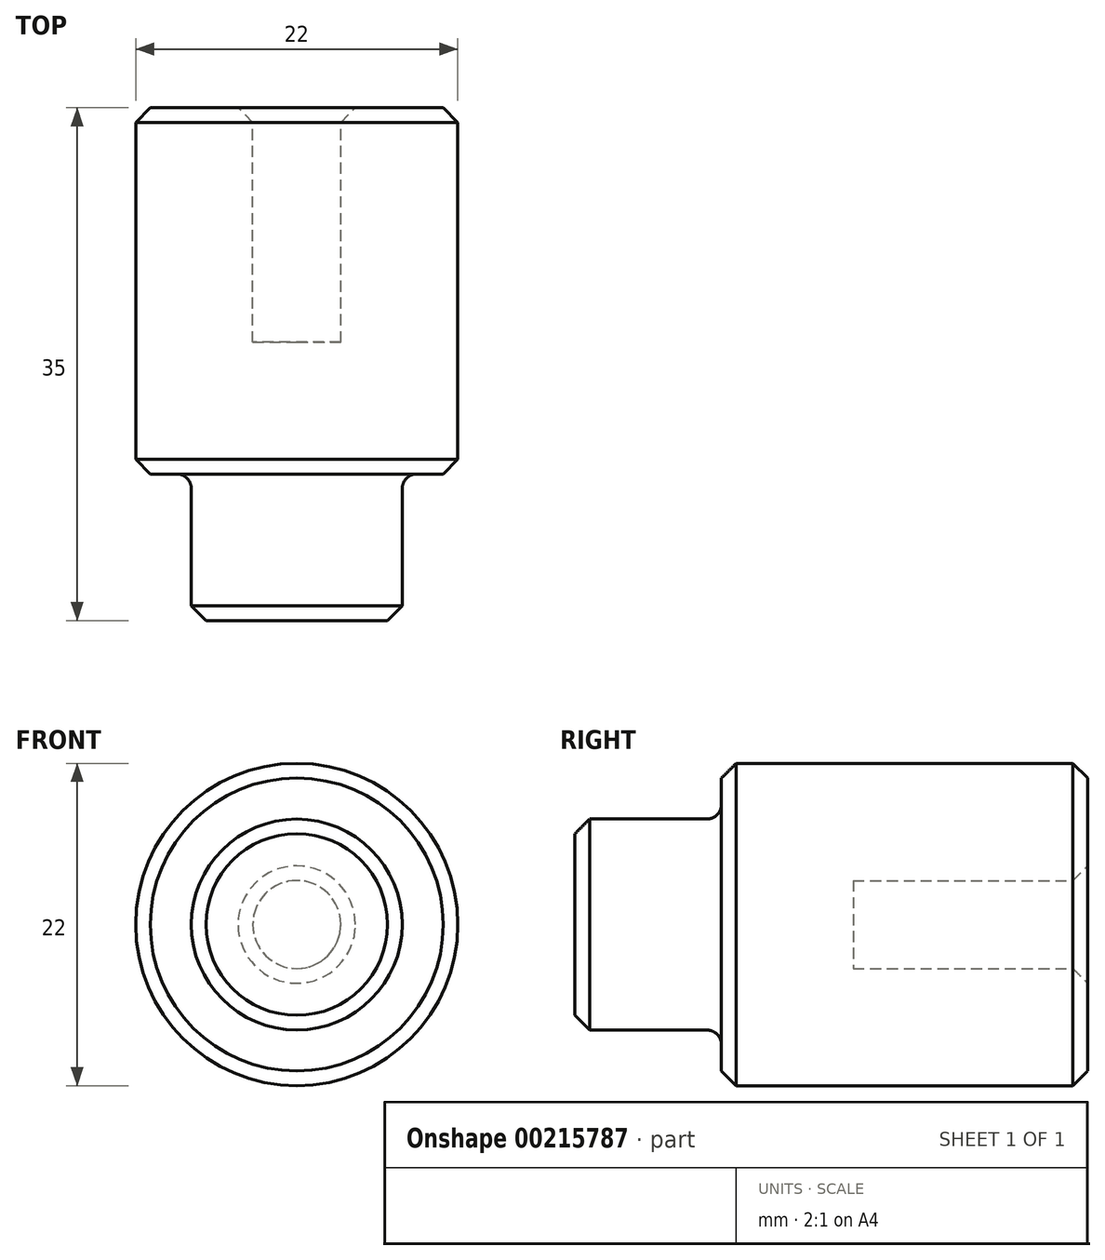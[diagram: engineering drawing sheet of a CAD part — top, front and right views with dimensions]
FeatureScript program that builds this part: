
annotation { "Feature Type Name" : "Feature", "Feature Type Description" : "" }
export const myFeature = defineFeature(function(context is Context, id is Id, definition is map)
    precondition{}
    {
        {
            var Q0;
            Q0=qCreatedBy(makeId("Right.planeOp"),FACE);
            var sketch = newSketch(context, id + "F0", { "sketchPlane" : qUnion([Q0])});
            skLineSegment(sketch, "E0", {"start": v(0, 0) * mm, "end": v(0, 7.2) * mm});
            skLineSegment(sketch, "E1", {"start": v(0, 7.2) * mm, "end": v(10, 7.2) * mm});
            skLineSegment(sketch, "E2", {"start": v(10, 7.2) * mm, "end": v(10, 11) * mm});
            skLineSegment(sketch, "E3", {"start": v(10, 11) * mm, "end": v(35, 11) * mm});
            skLineSegment(sketch, "E4", {"start": v(35, 11) * mm, "end": v(35, 3) * mm});
            skLineSegment(sketch, "E5", {"start": v(35, 3) * mm, "end": v(19, 3) * mm});
            skLineSegment(sketch, "E6", {"start": v(19, 3) * mm, "end": v(19, 0) * mm});
            skLineSegment(sketch, "E7", {"start": v(19, 0) * mm, "end": v(0, 0) * mm});
            skSolve(sketch);
        }
        {
            var Q0;
            Q0=makeQuery(id+"F0.imprint","IMPRINT",FACE,{"disambiguationData":[TD([[makeQuery(id+"F0.imprint","IMPRINT",EDGE,{"derivedFrom":sQuery(id+"F0.wireOp",EDGE,"E0")}),-1.0]])]});
            var Q1;
            Q1=sQuery(id+"F0.wireOp",EDGE,"E7");
            revolve(context, id + "F1", {"entities" : qUnion([Q0]), "axis" : qUnion([Q1]), "revolveType" : RevolveType.FULL});
        }
        {
            var Q0;
            Q0=makeQuery(id+"F1.opRevolve","SWEPT_EDGE",EDGE,{"disambiguationData":[OSD([sQuery(id+"F0.wireOp",EDGE,"E0"),sQuery(id+"F0.wireOp",EDGE,"E1")])]});
            var Q1;
            Q1=makeQuery(id+"F1.opRevolve","SWEPT_EDGE",EDGE,{"disambiguationData":[OSD([sQuery(id+"F0.wireOp",EDGE,"E2"),sQuery(id+"F0.wireOp",EDGE,"E3")])]});
            var Q2;
            Q2=makeQuery(id+"F1.opRevolve","SWEPT_EDGE",EDGE,{"disambiguationData":[OSD([sQuery(id+"F0.wireOp",EDGE,"E3"),sQuery(id+"F0.wireOp",EDGE,"E4")])]});
            var Q3;
            Q3=makeQuery(id+"F1.opRevolve","SWEPT_EDGE",EDGE,{"disambiguationData":[OSD([sQuery(id+"F0.wireOp",EDGE,"E4"),sQuery(id+"F0.wireOp",EDGE,"E5")])]});
            chamfer(context, id + "F2", {"entities" : qUnion([Q0, Q1, Q2, Q3]), "width" : 1 * mm, "tangentPropagation" : true});
        }
        {
            var Q0;
            Q0=makeQuery(id+"F1.opRevolve","SWEPT_EDGE",EDGE,{"disambiguationData":[OSD([sQuery(id+"F0.wireOp",EDGE,"E1"),sQuery(id+"F0.wireOp",EDGE,"E2")])]});
            fillet(context, id + "F3", {"entities" : qUnion([Q0]), "radius" : 1 * mm, "tangentPropagation" : true, "allowEdgeOverflow" : false});
        }
    });
